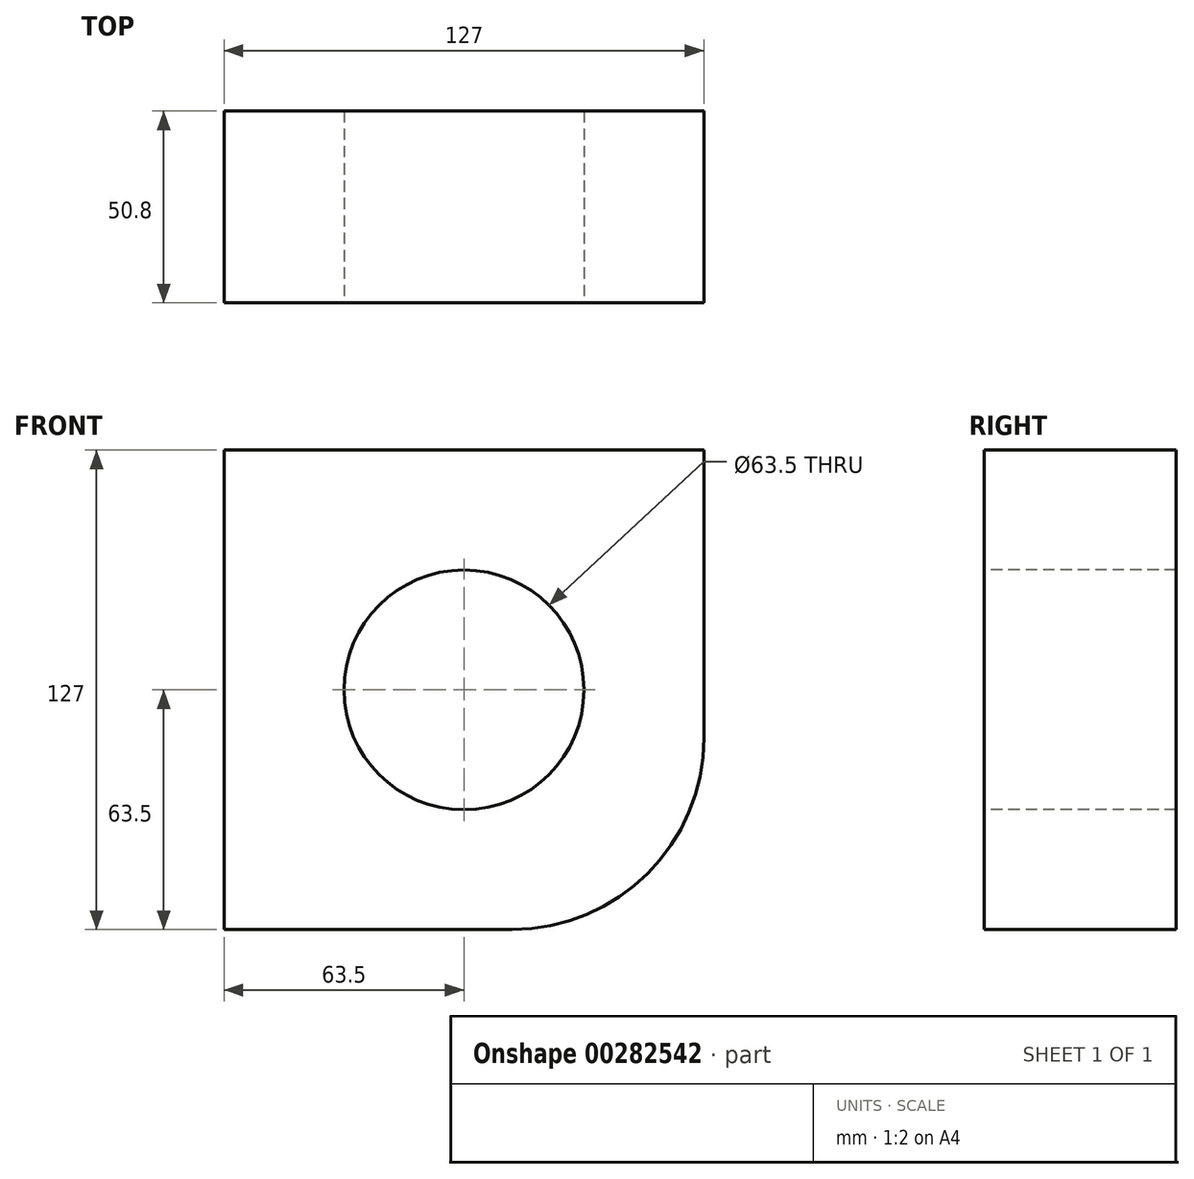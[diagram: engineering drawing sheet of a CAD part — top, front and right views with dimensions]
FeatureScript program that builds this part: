
annotation { "Feature Type Name" : "Feature", "Feature Type Description" : "" }
export const myFeature = defineFeature(function(context is Context, id is Id, definition is map)
    precondition{}
    {
        {
            var Q0;
            Q0=qCreatedBy(makeId("Top.planeOp"),FACE);
            var sketch = newSketch(context, id + "F0", { "sketchPlane" : qUnion([Q0])});
            skLineSegment(sketch, "E0.bottom", {"start": v(63.5, -25.4) * mm, "end": v(-63.5, -25.4) * mm});
            skLineSegment(sketch, "E0.top", {"start": v(63.5, 25.4) * mm, "end": v(-63.5, 25.4) * mm});
            skLineSegment(sketch, "E0.left", {"start": v(63.5, -25.4) * mm, "end": v(63.5, 25.4) * mm});
            skLineSegment(sketch, "E0.right", {"start": v(-63.5, -25.4) * mm, "end": v(-63.5, 25.4) * mm});
            skPoint(sketch, "E0.middle", {"position": v(0, 0) * mm});
            skSolve(sketch);
        }
        {
            var Q0;
            Q0 = qSketchRegion(id + "F0", true);
            extrude(context, id + "F1", {"entities" : qUnion([Q0]), "endBound" : BoundingType.SYMMETRIC, "depth" : 127 * mm});
        }
        {
            var Q0;
            Q0=makeQuery(id+"F1.opExtrude","CAP_EDGE",EDGE,{"disambiguationData":[OSD([sQuery(id+"F0.wireOp",EDGE,"E0.left")])],"isStart":true});
            fillet(context, id + "F2", {"entities" : qUnion([Q0]), "radius" : 50.8 * mm, "tangentPropagation" : true, "allowEdgeOverflow" : false});
        }
        {
            var Q0;
            Q0=makeQuery(id+"F1.opExtrude","SWEPT_FACE",FACE,{"disambiguationData":[OSD([sQuery(id+"F0.wireOp",EDGE,"E0.bottom")])]});
            var sketch = newSketch(context, id + "F3", { "sketchPlane" : qUnion([Q0])});
            skCircle(sketch, "E1", {"center": v(0, 0) * mm, "radius": 31.75 * mm});
            skSolve(sketch);
        }
        {
            var Q0;
            Q0 = qSketchRegion(id + "F3", true);
            extrude(context, id + "F4", {"entities" : qUnion([Q0]), "operationType" : NewBodyOperationType.REMOVE, "endBound" : BoundingType.THROUGH_ALL, "oppositeDirection" : true, "depth" : 25.4 * mm});
        }
    });
